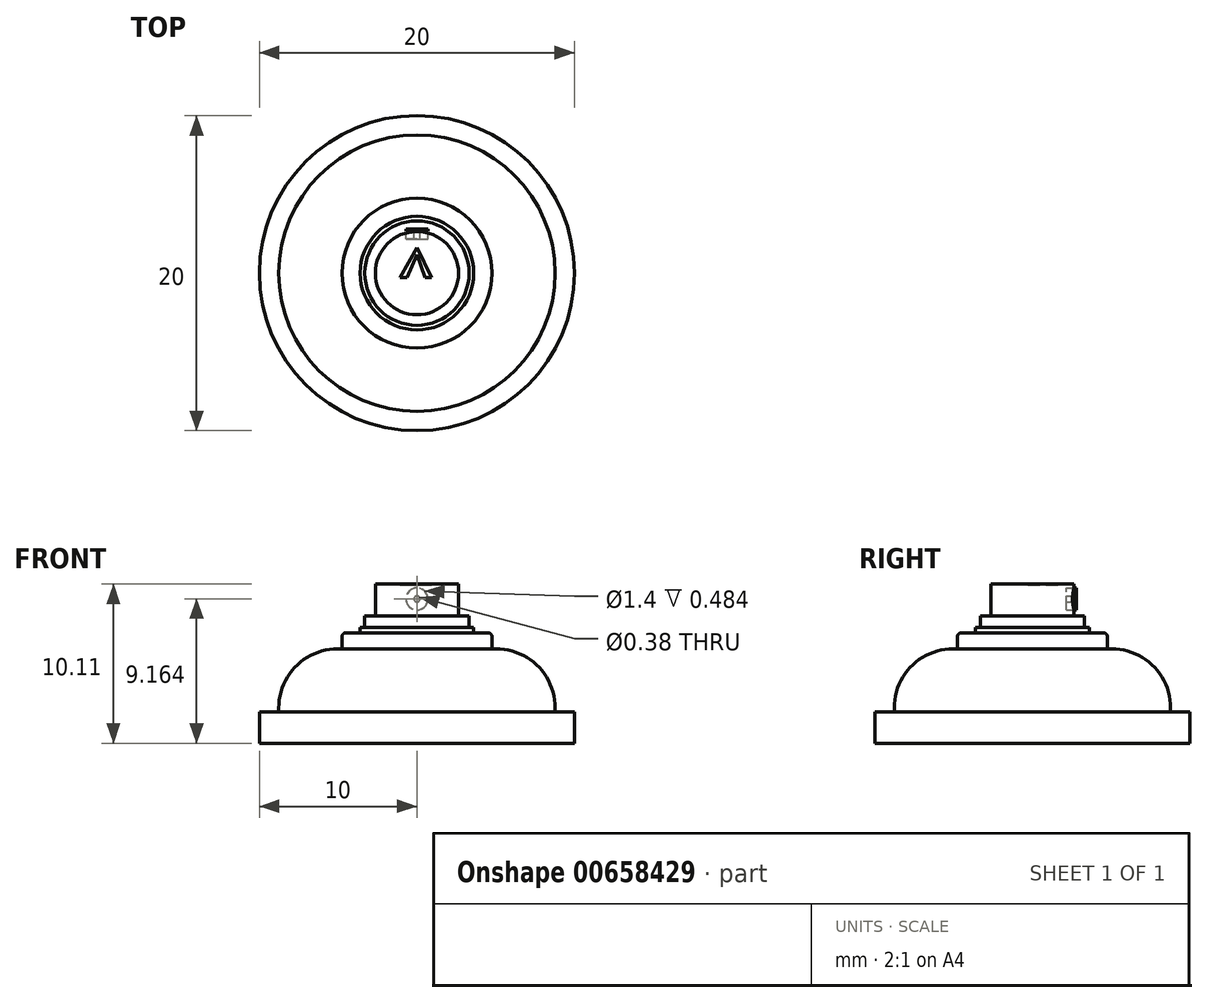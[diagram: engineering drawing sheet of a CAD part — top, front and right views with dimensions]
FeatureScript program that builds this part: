
annotation { "Feature Type Name" : "Feature", "Feature Type Description" : "" }
export const myFeature = defineFeature(function(context is Context, id is Id, definition is map)
    precondition{}
    {
        {
            var Q0;
            Q0=qCreatedBy(makeId("Top.planeOp"),FACE);
            var sketch = newSketch(context, id + "F0", { "sketchPlane" : qUnion([Q0])});
            skCircle(sketch, "E0", {"center": v(0, 0) * mm, "radius": 10 * mm});
            skPoint(sketch, "E1", {"position": v(-9.73, 2.32) * mm});
            skPoint(sketch, "E2", {"position": v(9.49, -3.18) * mm});
            skCircle(sketch, "E3", {"center": v(0, 0) * mm, "radius": 8.78 * mm});
            skCircle(sketch, "E4", {"center": v(0, 0) * mm, "radius": 3.6 * mm});
            skSolve(sketch);
        }
        {
            var Q0;
            Q0 = qSketchRegion(id + "F0", true);
            extrude(context, id + "F1", {"entities" : qUnion([Q0]), "depth" : 2 * mm, "offsetDistance" : 25.4 * mm});
        }
        {
            var Q0;
            Q0=makeQuery(id+"F0.imprint","IMPRINT",FACE,{"disambiguationData":[TD([[makeQuery(id+"F0.imprint","IMPRINT",EDGE,{"derivedFrom":sQuery(id+"F0.wireOp",EDGE,"E3")}),1.0]])]});
            var Q1;
            Q1=makeQuery(id+"F0.imprint","IMPRINT",FACE,{"disambiguationData":[TD([[makeQuery(id+"F0.imprint","IMPRINT",EDGE,{"derivedFrom":sQuery(id+"F0.wireOp",EDGE,"E4")}),1.0]])]});
            extrude(context, id + "F2", {"entities" : qUnion([Q0, Q1]), "operationType" : NewBodyOperationType.ADD, "depth" : 6 * mm, "offsetDistance" : 25.4 * mm});
        }
        {
            var Q0;
            Q0=makeQuery(id+"F0.imprint","IMPRINT",FACE,{"disambiguationData":[TD([[makeQuery(id+"F0.imprint","IMPRINT",EDGE,{"derivedFrom":sQuery(id+"F0.wireOp",EDGE,"E4")}),1.0]])]});
            extrude(context, id + "F3", {"entities" : qUnion([Q0]), "operationType" : NewBodyOperationType.ADD, "depth" : 10.1 * mm, "offsetDistance" : 25.4 * mm});
        }
        {
            var Q0;
            Q0=makeQuery(id+"F2.opExtrude","CAP_EDGE",EDGE,{"disambiguationData":[OSD([sQuery(id+"F0.wireOp",EDGE,"E3")])],"isStart":false});
            fillet(context, id + "F4", {"entities" : qUnion([Q0]), "radius" : 3.74 * mm, "tangentPropagation" : true, "allowEdgeOverflow" : false});
        }
        {
            var Q0;
            Q0=makeQuery(id+"F2.opExtrude","CAP_FACE",FACE,{"disambiguationData":[OSD([sQuery(id+"F0.wireOp",EDGE,"E3")])],"isStart":false});
            var sketch = newSketch(context, id + "F5", { "sketchPlane" : qUnion([Q0])});
            skCircle(sketch, "E5", {"center": v(0, 0) * mm, "radius": 4.76 * mm});
            skPoint(sketch, "E6", {"position": v(-4.76, 0) * mm});
            skPoint(sketch, "E7", {"position": v(4.76, 0) * mm});
            skSolve(sketch);
        }
        {
            var Q0;
            Q0 = qSketchRegion(id + "F5", true);
            extrude(context, id + "F6", {"entities" : qUnion([Q0]), "operationType" : NewBodyOperationType.ADD, "depth" : 1.02 * mm, "offsetDistance" : 25.4 * mm});
        }
        {
            var Q0;
            Q0=makeQuery(id+"F6.opExtrude","CAP_EDGE",EDGE,{"disambiguationData":[OSD([sQuery(id+"F5.wireOp",EDGE,"E5")])],"isStart":false});
            fillet(context, id + "F7", {"entities" : qUnion([Q0]), "radius" : 0.25 * mm, "tangentPropagation" : true, "allowEdgeOverflow" : false});
        }
        {
            var Q0;
            Q0=makeQuery(id+"F3.opExtrude","CAP_FACE",FACE,{"disambiguationData":[OSD([sQuery(id+"F0.wireOp",EDGE,"E4")])],"isStart":false});
            var sketch = newSketch(context, id + "F8", { "sketchPlane" : qUnion([Q0])});
            skCircle(sketch, "E8", {"center": v(0, 0) * mm, "radius": 3.31 * mm});
            skCircle(sketch, "E9", {"center": v(0, 0) * mm, "radius": 2.64 * mm});
            skPoint(sketch, "E10.end.orphan", {"position": v(-2.64, -0.04) * mm});
            skPoint(sketch, "E11.start.orphan", {"position": v(2.64, -0.04) * mm});
            skLineSegment(sketch, "E12", {"start": v(-1.07, -0.28) * mm, "end": v(0, 1.62) * mm});
            skLineSegment(sketch, "E13", {"start": v(0, 1.62) * mm, "end": v(0.94, -0.28) * mm});
            skLineSegment(sketch, "E14", {"start": v(-1.07, -0.28) * mm, "end": v(-0.64, -0.28) * mm});
            skLineSegment(sketch, "E15", {"start": v(-0.64, -0.28) * mm, "end": v(0, 1.2) * mm});
            skLineSegment(sketch, "E16", {"start": v(0, 1.2) * mm, "end": v(0.51, -0.28) * mm});
            skLineSegment(sketch, "E17.trimOffspring", {"start": v(0.51, -0.28) * mm, "end": v(0.94, -0.28) * mm});
            skPoint(sketch, "E18.orphan", {"position": v(0, -0.28) * mm});
            skSolve(sketch);
        }
        {
            var Q0;
            Q0=makeQuery(id+"F8.imprint","IMPRINT",FACE,{"disambiguationData":[TD([[makeQuery(id+"F8.imprint","IMPRINT",EDGE,{"derivedFrom":sQuery(id+"F8.wireOp",EDGE,"E8")}),-1.0]])]});
            extrude(context, id + "F9", {"entities" : qUnion([Q0]), "operationType" : NewBodyOperationType.REMOVE, "oppositeDirection" : true, "depth" : 2.77 * mm, "offsetDistance" : 25.4 * mm});
        }
        {
            var Q0;
            Q0=makeQuery(id+"F8.imprint","IMPRINT",FACE,{"disambiguationData":[TD([[makeQuery(id+"F8.imprint","IMPRINT",EDGE,{"derivedFrom":sQuery(id+"F8.wireOp",EDGE,"E8")}),1.0]])]});
            extrude(context, id + "F10", {"entities" : qUnion([Q0]), "operationType" : NewBodyOperationType.REMOVE, "oppositeDirection" : true, "depth" : 2.03 * mm, "offsetDistance" : 25.4 * mm});
        }
        {
            var Q0;
            Q0=qCreatedBy(makeId("Front.planeOp"),FACE);
            cPlane(context, id + "F11", {"entities" : qUnion([Q0]), "cplaneType" : CPlaneType.OFFSET, "offset" : 2.67 * mm, "oppositeDirection" : true, "width" : 152.4 * mm, "height" : 152.4 * mm});
        }
        {
            var Q0;
            Q0=qCreatedBy(id+"F11.planeOp",FACE);
            var sketch = newSketch(context, id + "F12", { "sketchPlane" : qUnion([Q0])});
            skLineSegment(sketch, "E19", {"start": v(0, 10.12) * mm, "end": v(0, 8.21) * mm});
            skCircle(sketch, "E20", {"center": v(0, 9.16) * mm, "radius": 0.7 * mm});
            skCircle(sketch, "E21", {"center": v(0, 9.16) * mm, "radius": 0.19 * mm});
            skSolve(sketch);
        }
        {
            var Q0;
            Q0 = qSketchRegion(id + "F12", true);
            extrude(context, id + "F13", {"entities" : qUnion([Q0]), "operationType" : NewBodyOperationType.ADD, "endBound" : BoundingType.SYMMETRIC, "depth" : 0.25 * mm, "offsetDistance" : 25.4 * mm});
        }
        {
            var Q0;
            {var subQ0=sQuery(id+"F12.wireOp",EDGE,"E21");var subQ1=sQuery(id+"F12.wireOp",EDGE,"E19");var subQ2=makeQuery(id+"F12.imprint","INTERSECT",VERTEX,{"disambiguationData":[OD(0.0)],"derivedFrom":[subQ1,subQ0]});Q0=makeQuery(id+"F12.imprint","IMPRINT",FACE,{"disambiguationData":[TD([[makeQuery(id+"F12.imprint","IMPRINT",EDGE,{"disambiguationData":[TD([[subQ2,-1.0]])],"derivedFrom":subQ1}),1.0]])]});}
            var Q1;
            {var subQ0=sQuery(id+"F12.wireOp",EDGE,"E21");var subQ1=sQuery(id+"F12.wireOp",EDGE,"E19");var subQ2=makeQuery(id+"F12.imprint","INTERSECT",VERTEX,{"disambiguationData":[OD(0.0)],"derivedFrom":[subQ1,subQ0]});Q1=makeQuery(id+"F12.imprint","IMPRINT",FACE,{"disambiguationData":[TD([[makeQuery(id+"F12.imprint","IMPRINT",EDGE,{"disambiguationData":[TD([[subQ2,-1.0]])],"derivedFrom":subQ1}),-1.0]])]});}
            extrude(context, id + "F14", {"entities" : qUnion([Q0, Q1]), "operationType" : NewBodyOperationType.REMOVE, "depth" : 0.5 * mm, "offsetDistance" : 25.4 * mm});
        }
        {
            var Q0;
            Q0=makeQuery(id+"F8.imprint","IMPRINT",FACE,{"disambiguationData":[TD([[makeQuery(id+"F8.imprint","IMPRINT",EDGE,{"derivedFrom":sQuery(id+"F8.wireOp",EDGE,"E12")}),-1.0]])]});
            extrude(context, id + "F15", {"entities" : qUnion([Q0]), "operationType" : NewBodyOperationType.REMOVE, "oppositeDirection" : true, "depth" : 0.05 * mm, "offsetDistance" : 25.4 * mm});
        }
    });
